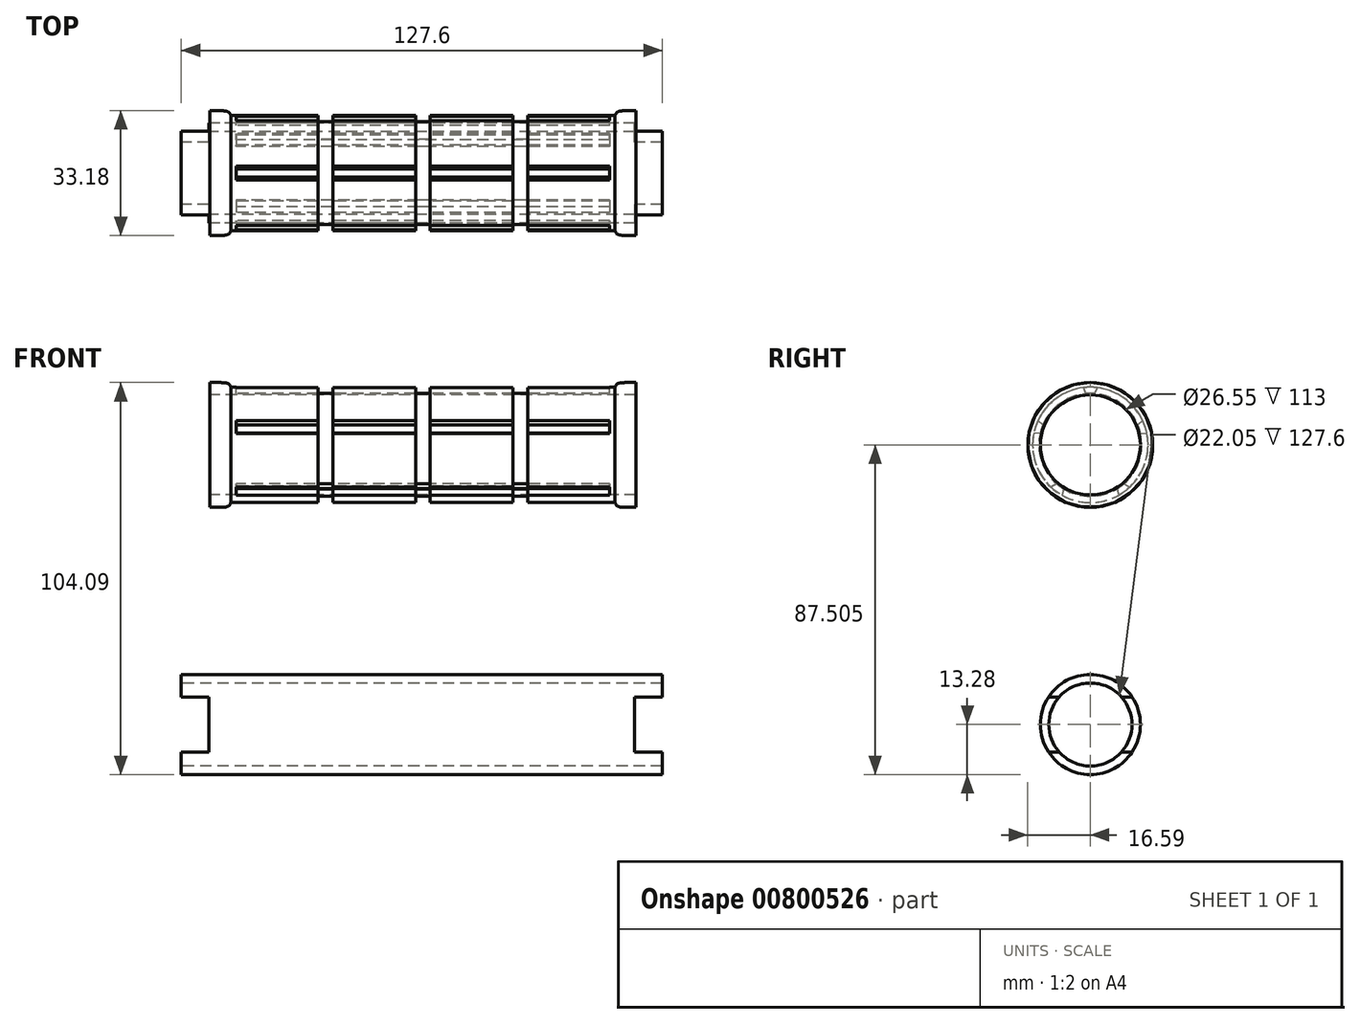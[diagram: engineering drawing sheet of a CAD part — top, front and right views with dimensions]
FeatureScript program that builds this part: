
annotation { "Feature Type Name" : "Feature", "Feature Type Description" : "" }
export const myFeature = defineFeature(function(context is Context, id is Id, definition is map)
    precondition{}
    {
        {
            var Q0;
            Q0=qCreatedBy(makeId("Front.planeOp"),FACE);
            var sketch = newSketch(context, id + "F0", { "sketchPlane" : qUnion([Q0])});
            skLineSegment(sketch, "E0", {"start": v(0, 0) * mm, "end": v(127.6, 0) * mm});
            skLineSegment(sketch, "E1", {"start": v(127.6, 0) * mm, "end": v(127.6, 11.02) * mm});
            skLineSegment(sketch, "E2", {"start": v(127.6, 11.03) * mm, "end": v(0, 11.03) * mm});
            skLineSegment(sketch, "E3", {"start": v(0, 11.03) * mm, "end": v(0, 0) * mm});
            skLineSegment(sketch, "E4", {"start": v(127.6, 11.02) * mm, "end": v(127.6, 13.28) * mm});
            skLineSegment(sketch, "E5", {"start": v(127.6, 13.28) * mm, "end": v(0, 13.28) * mm});
            skLineSegment(sketch, "E6", {"start": v(0, 13.28) * mm, "end": v(0, 11.03) * mm});
            skLineSegment(sketch, "E7.MirrorCS", {"start": v(127.6, -11.03) * mm, "end": v(0, -11.03) * mm});
            skLineSegment(sketch, "E8.MirrorCS", {"start": v(127.6, -13.28) * mm, "end": v(0, -13.28) * mm});
            skLineSegment(sketch, "E9.MirrorCS", {"start": v(127.6, -11.02) * mm, "end": v(127.6, -13.28) * mm});
            skLineSegment(sketch, "E10.MirrorCS", {"start": v(0, -13.28) * mm, "end": v(0, -11.03) * mm});
            skSolve(sketch);
        }
        {
            var Q0;
            Q0=makeQuery(id+"F0.imprint","IMPRINT",FACE,{"disambiguationData":[TD([[makeQuery(id+"F0.imprint","IMPRINT",EDGE,{"derivedFrom":sQuery(id+"F0.wireOp",EDGE,"E2")}),-1.0]])]});
            var Q1;
            Q1=sQuery(id+"F0.wireOp",EDGE,"E0");
            revolve(context, id + "F1", {"surfaceOperationType" : NewSurfaceOperationType.NEW, "entities" : qUnion([Q0]), "axis" : qUnion([Q1]), "revolveType" : RevolveType.FULL});
        }
        {
            var Q0;
            Q0=qCreatedBy(makeId("Front.planeOp"),FACE);
            var sketch = newSketch(context, id + "F2", { "sketchPlane" : qUnion([Q0])});
            skLineSegment(sketch, "E11", {"start": v(7.3, 0) * mm, "end": v(120.3, 0) * mm});
            skLineSegment(sketch, "E12", {"start": v(120.3, 0) * mm, "end": v(120.3, 7.3) * mm});
            skLineSegment(sketch, "E13", {"start": v(120.3, 7.3) * mm, "end": v(131.8, 7.3) * mm});
            skLineSegment(sketch, "E14", {"start": v(131.8, 7.3) * mm, "end": v(131.8, 0) * mm});
            skLineSegment(sketch, "E15", {"start": v(120.3, 7.3) * mm, "end": v(120.3, 0) * mm});
            skLineSegment(sketch, "E16", {"start": v(120.3, 7.3) * mm, "end": v(120.3, 0.33) * mm});
            skLineSegment(sketch, "E17", {"start": v(63.8, 0) * mm, "end": v(63.8, 23.73) * mm});
            skLineSegment(sketch, "E18.MirrorCS", {"start": v(7.3, 7.3) * mm, "end": v(7.3, 0) * mm});
            skLineSegment(sketch, "E19.MirrorCS", {"start": v(7.3, 7.3) * mm, "end": v(-4.2, 7.3) * mm});
            skLineSegment(sketch, "E20.MirrorCS", {"start": v(-4.2, 7.3) * mm, "end": v(-4.2, 0) * mm});
            skLineSegment(sketch, "E21.MirrorCS", {"start": v(120.3, -7.3) * mm, "end": v(131.8, -7.3) * mm});
            skLineSegment(sketch, "E22.MirrorCS", {"start": v(131.8, -7.3) * mm, "end": v(131.8, 0) * mm});
            skLineSegment(sketch, "E23.MirrorCS", {"start": v(120.3, -7.3) * mm, "end": v(120.3, 0) * mm});
            skLineSegment(sketch, "E24.MirrorCS", {"start": v(7.3, -7.3) * mm, "end": v(-4.2, -7.3) * mm});
            skLineSegment(sketch, "E25.MirrorCS", {"start": v(7.3, -7.3) * mm, "end": v(7.3, 0) * mm});
            skLineSegment(sketch, "E26.MirrorCS", {"start": v(-4.2, -7.3) * mm, "end": v(-4.2, 0) * mm});
            skPoint(sketch, "E27.MirrorCS.end.orphan", {"position": v(7.3, 0) * mm});
            skPoint(sketch, "E27.MirrorCS.start.orphan", {"position": v(-4.2, 0) * mm});
            skLineSegment(sketch, "E28", {"start": v(0, 34.45) * mm, "end": v(7.3, 34.45) * mm});
            skLineSegment(sketch, "E29", {"start": v(7.3, 49.55) * mm, "end": v(116.95, 49.55) * mm});
            skLineSegment(sketch, "E30", {"start": v(116.95, 49.55) * mm, "end": v(116.95, 45.9) * mm});
            skLineSegment(sketch, "E31", {"start": v(116.95, 45.9) * mm, "end": v(116.95, 34.45) * mm});
            skLineSegment(sketch, "E32", {"start": v(116.95, 34.45) * mm, "end": v(116.95, 45.9) * mm});
            skLineSegment(sketch, "E33.MirrorCS", {"start": v(7.3, 19.35) * mm, "end": v(116.95, 19.35) * mm});
            skLineSegment(sketch, "E34.MirrorCS", {"start": v(116.95, 19.35) * mm, "end": v(116.95, 23) * mm});
            skPoint(sketch, "E35.MirrorCS.end.orphan", {"position": v(7.3, 23) * mm});
            skPoint(sketch, "E35.MirrorCS.start.orphan", {"position": v(7.3, 34.45) * mm});
            skPoint(sketch, "E36.MirrorCS.end.orphan", {"position": v(116.95, 34.45) * mm});
            skPoint(sketch, "E36.MirrorCS.start.orphan", {"position": v(116.95, 23) * mm});
            skLineSegment(sketch, "E37", {"start": v(7.3, 45.9) * mm, "end": v(116.95, 45.9) * mm});
            skLineSegment(sketch, "E38", {"start": v(7.3, 49.55) * mm, "end": v(7.3, 50.89) * mm});
            skLineSegment(sketch, "E39.MirrorCS", {"start": v(7.3, 19.35) * mm, "end": v(7.3, 18) * mm});
            skPoint(sketch, "E40.MirrorCS.end.orphan", {"position": v(7.3, 19.35) * mm});
            skSolve(sketch);
        }
        {
            var Q0;
            Q0 = qSketchRegion(id + "F2", true);
            extrude(context, id + "F3", {"entities" : qUnion([Q0]), "operationType" : NewBodyOperationType.REMOVE, "endBound" : BoundingType.SYMMETRIC, "oppositeDirection" : true, "depth" : 30 * mm, "offsetDistance" : 25 * mm});
        }
        {
            var Q0;
            Q0=qCreatedBy(makeId("Front.planeOp"),FACE);
            var sketch = newSketch(context, id + "F4", { "sketchPlane" : qUnion([Q0])});
            skLineSegment(sketch, "E41", {"start": v(7.62, 74.22) * mm, "end": v(120.62, 74.22) * mm});
            skLineSegment(sketch, "E42", {"start": v(7.62, 74.22) * mm, "end": v(7.62, 87.5) * mm});
            skPoint(sketch, "E43.start.orphan", {"position": v(0, 73.16) * mm});
            skLineSegment(sketch, "E44", {"start": v(7.62, 87.5) * mm, "end": v(120.62, 87.5) * mm});
            skLineSegment(sketch, "E45", {"start": v(120.62, 87.5) * mm, "end": v(120.62, 89.54) * mm});
            skLineSegment(sketch, "E46", {"start": v(120.62, 89.54) * mm, "end": v(7.62, 89.54) * mm});
            skLineSegment(sketch, "E47", {"start": v(7.62, 89.54) * mm, "end": v(7.62, 87.5) * mm});
            skLineSegment(sketch, "E48.MirrorCS", {"start": v(7.62, 60.95) * mm, "end": v(120.62, 60.95) * mm});
            skLineSegment(sketch, "E49.MirrorCS", {"start": v(115.07, 58.9) * mm, "end": v(91.92, 58.9) * mm});
            skLineSegment(sketch, "E50.MirrorCS", {"start": v(120.62, 60.95) * mm, "end": v(120.62, 58.9) * mm});
            skLineSegment(sketch, "E51.MirrorCS", {"start": v(7.62, 58.9) * mm, "end": v(7.62, 60.95) * mm});
            skLineSegment(sketch, "E52", {"start": v(120.62, 89.54) * mm, "end": v(120.62, 90.78) * mm});
            skLineSegment(sketch, "E53.MirrorCS", {"start": v(120.62, 58.9) * mm, "end": v(120.62, 57.66) * mm});
            skLineSegment(sketch, "E54", {"start": v(120.62, 89.54) * mm, "end": v(115.07, 89.54) * mm});
            skFitSpline(sketch, "E55", {"points": [v(120.62, 90.78) * mm, v(117.54, 90.78) * mm, v(115.66, 90.41) * mm, v(115.07, 89.54) * mm], "startDerivative": vector(-8.6, 0.22) * mm, "endDerivative": vector(-2.24, -3.96) * mm});
            skPoint(sketch, "E56", {"position": v(120.62, 87.87) * mm});
            skLineSegment(sketch, "E57", {"start": v(64.12, 74.22) * mm, "end": v(64.12, 83.94) * mm});
            skFitSpline(sketch, "E58.MirrorCS", {"points": [v(120.62, 57.66) * mm, v(117.54, 57.66) * mm, v(115.66, 58.04) * mm, v(115.07, 58.9) * mm], "startDerivative": vector(-8.6, -0.22) * mm, "endDerivative": vector(-2.24, 3.96) * mm});
            skPoint(sketch, "E59.MirrorP", {"position": v(120.62, 60.57) * mm});
            skLineSegment(sketch, "E60", {"start": v(91.92, 60.57) * mm, "end": v(88.02, 60.57) * mm});
            skPoint(sketch, "E61", {"position": v(91.92, 60.57) * mm});
            skPoint(sketch, "E62", {"position": v(88.02, 60.57) * mm});
            skLineSegment(sketch, "E63", {"start": v(91.92, 60.57) * mm, "end": v(91.92, 58.9) * mm});
            skLineSegment(sketch, "E64", {"start": v(88.02, 60.57) * mm, "end": v(88.02, 58.9) * mm});
            skPoint(sketch, "E65.endSnap0", {"position": v(64.12, 58.9) * mm});
            skLineSegment(sketch, "E66.MirrorCS", {"start": v(36.32, 60.57) * mm, "end": v(36.32, 58.9) * mm});
            skLineSegment(sketch, "E67.MirrorCS", {"start": v(40.22, 60.57) * mm, "end": v(40.22, 58.9) * mm});
            skLineSegment(sketch, "E68.trimOffspring", {"start": v(36.32, 58.9) * mm, "end": v(13.17, 58.9) * mm});
            skLineSegment(sketch, "E69.trimOffspring", {"start": v(88.02, 58.9) * mm, "end": v(66.07, 58.9) * mm});
            skLineSegment(sketch, "E70", {"start": v(66.07, 58.9) * mm, "end": v(66.07, 60.57) * mm});
            skLineSegment(sketch, "E71.MirrorCS", {"start": v(62.17, 58.9) * mm, "end": v(62.17, 60.57) * mm});
            skLineSegment(sketch, "E72.trimOffspring", {"start": v(62.17, 58.9) * mm, "end": v(40.22, 58.9) * mm});
            skLineSegment(sketch, "E73.trimOffspring", {"start": v(64.12, 58.9) * mm, "end": v(64.12, 58.9) * mm});
            skFitSpline(sketch, "E74.MirrorCS", {"points": [v(7.62, 57.66) * mm, v(10.7, 57.66) * mm, v(12.57, 58.04) * mm, v(13.17, 58.9) * mm], "startDerivative": vector(8.6, -0.22) * mm, "endDerivative": vector(2.24, 3.96) * mm});
            skLineSegment(sketch, "E75.trimOffspring", {"start": v(66.07, 60.57) * mm, "end": v(62.17, 60.57) * mm});
            skLineSegment(sketch, "E76.trimOffspring", {"start": v(40.22, 60.57) * mm, "end": v(36.32, 60.57) * mm});
            skPoint(sketch, "E77.orphan", {"position": v(7.62, 58.9) * mm});
            skPoint(sketch, "E78.orphan", {"position": v(120.62, 58.9) * mm});
            skLineSegment(sketch, "E79", {"start": v(7.62, 58.9) * mm, "end": v(7.62, 57.66) * mm});
            skLineSegment(sketch, "E80.MirrorCS", {"start": v(40.22, 87.87) * mm, "end": v(36.32, 87.87) * mm});
            skSolve(sketch);
        }
        {
            var Q0;
            Q0=makeQuery(id+"F4.imprint","IMPRINT",FACE,{"disambiguationData":[TD([[makeQuery(id+"F4.imprint","IMPRINT",EDGE,{"derivedFrom":sQuery(id+"F4.wireOp",EDGE,"E48.MirrorCS")}),-1.0]])]});
            var Q1;
            Q1=sQuery(id+"F4.wireOp",EDGE,"E41");
            revolve(context, id + "F5", {"surfaceOperationType" : NewSurfaceOperationType.NEW, "entities" : qUnion([Q0]), "axis" : qUnion([Q1]), "revolveType" : RevolveType.FULL});
        }
        {
            var Q0;
            Q0=makeQuery(id+"F5.opRevolve","SWEPT_FACE",FACE,{"disambiguationData":[OSD([sQuery(id+"F4.wireOp",EDGE,"E70")])]});
            cPlane(context, id + "F6", {"entities" : qUnion([Q0]), "cplaneType" : CPlaneType.OFFSET, "offset" : 1.95 * mm, "width" : 150 * mm, "height" : 150 * mm});
        }
        {
            var Q0;
            Q0=qCreatedBy(id+"F6.planeOp",FACE);
            var sketch = newSketch(context, id + "F7", { "sketchPlane" : qUnion([Q0])});
            skLineSegment(sketch, "E81", {"start": v(0, 74.26) * mm, "end": v(0, 87.9) * mm});
            skPoint(sketch, "E82", {"position": v(-1.1, 87.86) * mm});
            skPoint(sketch, "E83.MirrorP", {"position": v(1.1, 87.86) * mm});
            skLineSegment(sketch, "E84", {"start": v(0, 89.57) * mm, "end": v(0, 90.76) * mm});
            skPoint(sketch, "E85", {"position": v(-1.85, 89.46) * mm});
            skPoint(sketch, "E86", {"position": v(0, 89.57) * mm});
            skPoint(sketch, "E87.MirrorP", {"position": v(1.85, 89.46) * mm});
            skLineSegment(sketch, "E88", {"start": v(1.1, 87.86) * mm, "end": v(1.85, 89.46) * mm});
            skLineSegment(sketch, "E89", {"start": v(-1.1, 87.86) * mm, "end": v(-1.85, 89.46) * mm});
            skLineSegment(sketch, "E90.1.0", {"start": v(-12.6, 79.5) * mm, "end": v(-13.89, 80.71) * mm});
            skLineSegment(sketch, "E90.1.1", {"start": v(-29.63, 88.7) * mm, "end": v(-29.63, 88.7) * mm});
            skLineSegment(sketch, "E90.2.0", {"start": v(-8.89, 63.9) * mm, "end": v(-10.43, 63.05) * mm});
            skLineSegment(sketch, "E90.2.1", {"start": v(-7.1, 62.6) * mm, "end": v(-7.44, 60.87) * mm});
            skLineSegment(sketch, "E90.3.0", {"start": v(7.1, 62.6) * mm, "end": v(7.44, 60.87) * mm});
            skLineSegment(sketch, "E90.3.1", {"start": v(8.89, 63.9) * mm, "end": v(10.43, 63.05) * mm});
            skLineSegment(sketch, "E90.4.0", {"start": v(13.28, 77.42) * mm, "end": v(15.03, 77.2) * mm});
            skLineSegment(sketch, "E90.4.1", {"start": v(12.6, 79.5) * mm, "end": v(13.89, 80.71) * mm});
            skPoint(sketch, "E90.center", {"position": v(0, 74.26) * mm});
            skArc(sketch, "E91", {"start": v(1.1, 87.86) * mm, "mid": v(0, 87.9) * mm, "end": v(-1.1, 87.86) * mm});
            skArc(sketch, "E92", {"start": v(13.28, 77.42) * mm, "mid": v(12.98, 78.48) * mm, "end": v(12.6, 79.5) * mm});
            skLineSegment(sketch, "E93", {"start": v(-3.07, 88.7) * mm, "end": v(-3.07, 88.7) * mm});
            skArc(sketch, "E94", {"start": v(7.1, 62.6) * mm, "mid": v(8.02, 63.21) * mm, "end": v(8.89, 63.9) * mm});
            skArc(sketch, "E95", {"start": v(-8.89, 63.9) * mm, "mid": v(-8.02, 63.21) * mm, "end": v(-7.1, 62.6) * mm});
            skLineSegment(sketch, "E96", {"start": v(-13.28, 77.42) * mm, "end": v(-15.03, 77.2) * mm});
            skArc(sketch, "E97", {"start": v(-12.6, 79.5) * mm, "mid": v(-12.98, 78.48) * mm, "end": v(-13.28, 77.42) * mm});
            skArc(sketch, "E98", {"start": v(13.89, 80.71) * mm, "mid": v(9, 86.65) * mm, "end": v(1.85, 89.46) * mm, "construction": true});
            skArc(sketch, "E99", {"start": v(15.03, 77.2) * mm, "mid": v(14.57, 79) * mm, "end": v(13.89, 80.71) * mm});
            skArc(sketch, "E100", {"start": v(10.43, 63.05) * mm, "mid": v(14.57, 69.52) * mm, "end": v(15.03, 77.2) * mm, "construction": true});
            skArc(sketch, "E101", {"start": v(-7.44, 60.87) * mm, "mid": v(0, 58.94) * mm, "end": v(7.44, 60.87) * mm, "construction": true});
            skArc(sketch, "E102", {"start": v(-15.03, 77.2) * mm, "mid": v(-14.57, 69.52) * mm, "end": v(-10.43, 63.05) * mm, "construction": true});
            skArc(sketch, "E103", {"start": v(-13.89, 80.71) * mm, "mid": v(-14.57, 79) * mm, "end": v(-15.03, 77.2) * mm});
            skArc(sketch, "E104", {"start": v(1.85, 89.46) * mm, "mid": v(0, 89.57) * mm, "end": v(-1.85, 89.46) * mm});
            skArc(sketch, "E105", {"start": v(-1.85, 89.46) * mm, "mid": v(-9, 86.65) * mm, "end": v(-13.89, 80.71) * mm, "construction": true});
            skLineSegment(sketch, "E106", {"start": v(-10.05, 63.25) * mm, "end": v(-12.24, 62.23) * mm});
            skLineSegment(sketch, "E107", {"start": v(-7.32, 61.49) * mm, "end": v(-7.84, 58.76) * mm});
            skLineSegment(sketch, "E108", {"start": v(-7.84, 58.76) * mm, "end": v(-12.24, 62.23) * mm});
            skLineSegment(sketch, "E109", {"start": v(7.32, 61.5) * mm, "end": v(8, 58) * mm});
            skLineSegment(sketch, "E110", {"start": v(8, 58) * mm, "end": v(12.54, 61.89) * mm});
            skLineSegment(sketch, "E111", {"start": v(9.97, 63.3) * mm, "end": v(12.54, 61.89) * mm});
            skSolve(sketch);
        }
        {
            var Q0;
            Q0 = qSketchRegion(id + "F7", true);
            extrude(context, id + "F8", {"entities" : qUnion([Q0]), "operationType" : NewBodyOperationType.REMOVE, "endBound" : BoundingType.SYMMETRIC, "oppositeDirection" : true, "depth" : 99.14 * mm, "offsetDistance" : 25 * mm});
        }
    });
